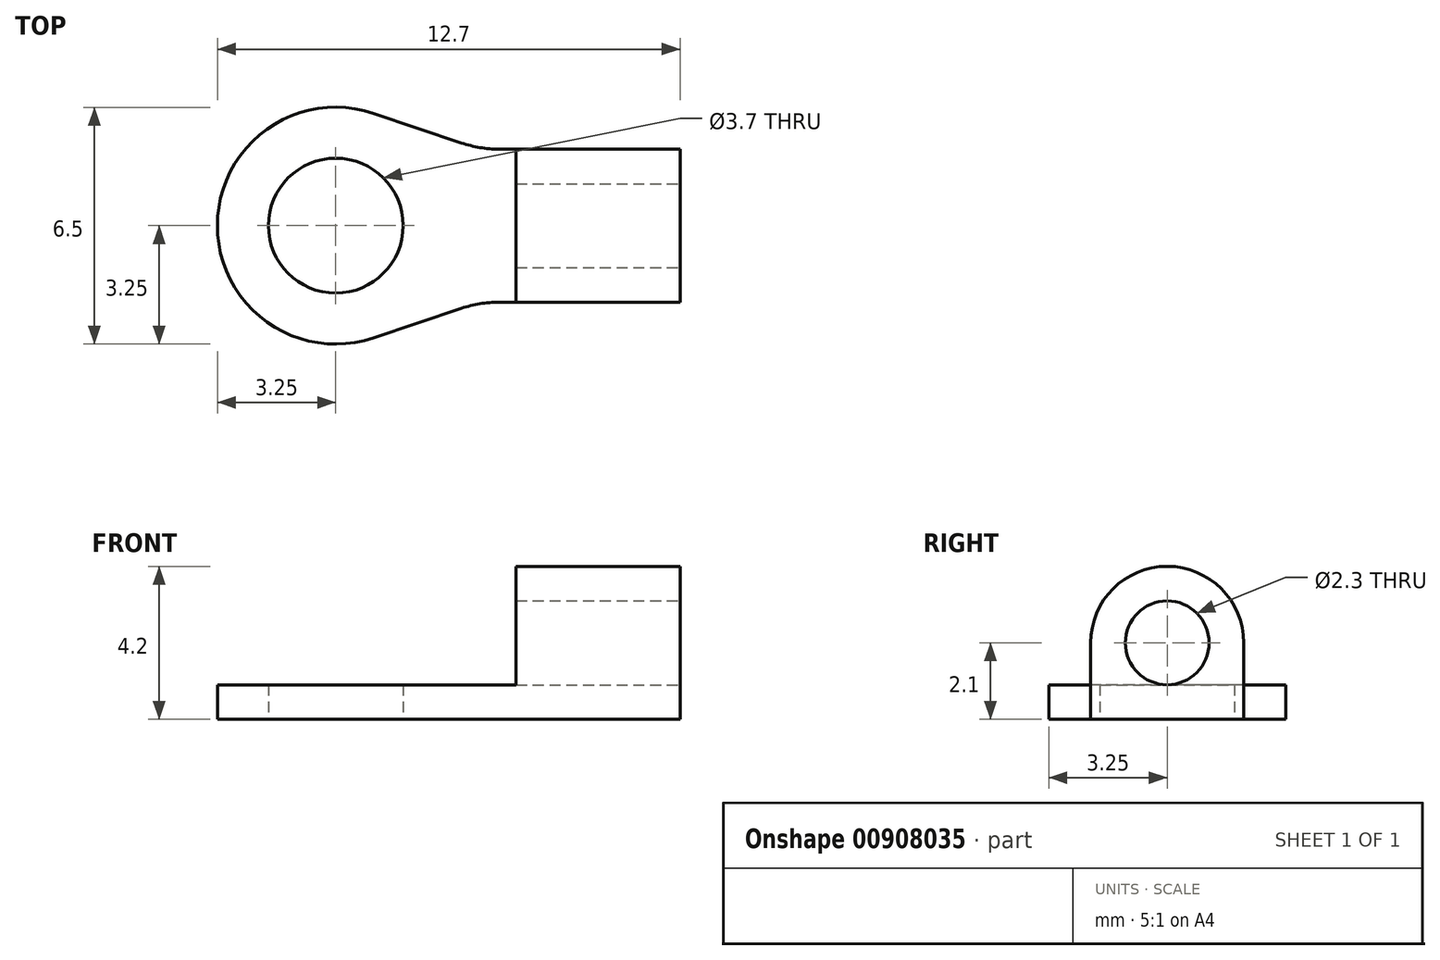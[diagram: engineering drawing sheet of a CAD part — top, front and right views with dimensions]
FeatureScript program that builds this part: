
annotation { "Feature Type Name" : "Feature", "Feature Type Description" : "" }
export const myFeature = defineFeature(function(context is Context, id is Id, definition is map)
    precondition{}
    {
        {
            var Q0;
            Q0=qCreatedBy(makeId("Top.planeOp"),FACE);
            var sketch = newSketch(context, id + "F0", { "sketchPlane" : qUnion([Q0])});
            skLineSegment(sketch, "E0.left", {"start": v(0, 3.25) * mm, "end": v(0, 3.25) * mm});
            skLineSegment(sketch, "E0.right", {"start": v(12.7, 1.15) * mm, "end": v(12.7, 5.35) * mm});
            skPoint(sketch, "E1.visualSharp", {"position": v(0, 6.5) * mm});
            skArc(sketch, "E1.filletArc", {"start": v(3.25, 6.5) * mm, "mid": v(0.95, 5.55) * mm, "end": v(0, 3.25) * mm});
            skPoint(sketch, "E2.visualSharp", {"position": v(0, 0) * mm});
            skArc(sketch, "E2.filletArc", {"start": v(0, 3.25) * mm, "mid": v(0.95, 0.95) * mm, "end": v(3.25, 0) * mm});
            skLineSegment(sketch, "E3.bottom", {"start": v(12.7, 1.15) * mm, "end": v(8.2, 1.15) * mm});
            skLineSegment(sketch, "E3.top", {"start": v(12.7, 5.35) * mm, "end": v(8.2, 5.35) * mm});
            skPoint(sketch, "E3.middle", {"position": v(12.7, 3.25) * mm});
            skArc(sketch, "E4", {"start": v(4.29, 6.33) * mm, "mid": v(0, 3.25) * mm, "end": v(4.29, 0.17) * mm});
            skCircle(sketch, "E5", {"center": v(3.25, 3.25) * mm, "radius": 1.85 * mm});
            skLineSegment(sketch, "E6", {"start": v(8.2, 5.35) * mm, "end": v(7.73, 5.35) * mm});
            skLineSegment(sketch, "E7", {"start": v(7.73, 1.15) * mm, "end": v(8.2, 1.15) * mm});
            skLineSegment(sketch, "E8", {"start": v(6.7, 5.52) * mm, "end": v(4.29, 6.33) * mm});
            skLineSegment(sketch, "E9", {"start": v(6.7, 0.98) * mm, "end": v(4.29, 0.17) * mm});
            skPoint(sketch, "E10.orphan", {"position": v(17.2, 5.35) * mm});
            skPoint(sketch, "E11.orphan", {"position": v(17.2, 1.15) * mm});
            skPoint(sketch, "E0.top.end.orphan", {"position": v(12.7, 6.5) * mm});
            skPoint(sketch, "E0.bottom.end.orphan", {"position": v(12.7, 0) * mm});
            skPoint(sketch, "E12.visualSharp", {"position": v(7.2, 5.35) * mm});
            skArc(sketch, "E12.filletArc", {"start": v(6.7, 5.52) * mm, "mid": v(7.2, 5.4) * mm, "end": v(7.73, 5.35) * mm});
            skPoint(sketch, "E13.visualSharp", {"position": v(7.2, 1.15) * mm});
            skArc(sketch, "E13.filletArc", {"start": v(7.73, 1.15) * mm, "mid": v(7.2, 1.1) * mm, "end": v(6.7, 0.98) * mm});
            skSolve(sketch);
        }
        {
            var Q0;
            Q0=makeQuery(id+"F0.imprint","IMPRINT",FACE,{"disambiguationData":[TD([[makeQuery(id+"F0.imprint","IMPRINT",EDGE,{"derivedFrom":sQuery(id+"F0.wireOp",EDGE,"E0.right")}),1.0]])]});
            extrude(context, id + "F1", {"entities" : qUnion([Q0]), "depth" : 0.95 * mm, "offsetDistance" : 25 * mm});
        }
        {
            var Q0;
            Q0=makeQuery(id+"F1.opExtrude","CAP_FACE",FACE,{"disambiguationData":[OSD([sQuery(id+"F0.wireOp",EDGE,"E0.right"),sQuery(id+"F0.wireOp",EDGE,"E3.bottom"),sQuery(id+"F0.wireOp",EDGE,"E3.top"),sQuery(id+"F0.wireOp",EDGE,"E4"),sQuery(id+"F0.wireOp",EDGE,"E5"),sQuery(id+"F0.wireOp",EDGE,"E6"),sQuery(id+"F0.wireOp",EDGE,"E7"),sQuery(id+"F0.wireOp",EDGE,"E8"),sQuery(id+"F0.wireOp",EDGE,"E9"),sQuery(id+"F0.wireOp",EDGE,"E12.filletArc"),sQuery(id+"F0.wireOp",EDGE,"E13.filletArc")])],"isStart":false});
            var sketch = newSketch(context, id + "F2", { "sketchPlane" : qUnion([Q0])});
            skLineSegment(sketch, "E14.bottom", {"start": v(12.7, 5.35) * mm, "end": v(8.2, 5.35) * mm});
            skLineSegment(sketch, "E14.top", {"start": v(12.7, 1.15) * mm, "end": v(8.2, 1.15) * mm});
            skLineSegment(sketch, "E14.left", {"start": v(12.7, 5.35) * mm, "end": v(12.7, 1.15) * mm});
            skLineSegment(sketch, "E14.right", {"start": v(8.2, 5.35) * mm, "end": v(8.2, 1.15) * mm});
            skSolve(sketch);
        }
        {
            var Q0;
            Q0=makeQuery(id+"F2.imprint","IMPRINT",FACE,{"disambiguationData":[TD([[makeQuery(id+"F2.imprint","IMPRINT",EDGE,{"derivedFrom":sQuery(id+"F2.wireOp",EDGE,"E14.bottom")}),1.0]])]});
            extrude(context, id + "F3", {"entities" : qUnion([Q0]), "operationType" : NewBodyOperationType.ADD, "depth" : 3.25 * mm, "offsetDistance" : 25 * mm});
        }
        {
            var Q0;
            Q0=makeQuery(id+"F3.opExtrude","CAP_EDGE",EDGE,{"disambiguationData":[OSD([sQuery(id+"F2.wireOp",EDGE,"E14.bottom")])],"isStart":false});
            var Q1;
            Q1=makeQuery(id+"F3.opExtrude","CAP_EDGE",EDGE,{"disambiguationData":[OSD([sQuery(id+"F2.wireOp",EDGE,"E14.top")])],"isStart":false});
            fillet(context, id + "F4", {"entities" : qUnion([Q0, Q1]), "radius" : 2.1 * mm, "tangentPropagation" : true, "allowEdgeOverflow" : false});
        }
        {
            var Q0;
            Q0=makeQuery(id+"F3.boolean.opBoolean","MERGE",FACE,{"derivedFrom":[makeQuery(id+"F1.opExtrude","SWEPT_FACE",FACE,{"disambiguationData":[OSD([sQuery(id+"F0.wireOp",EDGE,"E0.right")])]}),makeQuery(id+"F3.opExtrude","SWEPT_FACE",FACE,{"disambiguationData":[OSD([sQuery(id+"F2.wireOp",EDGE,"E14.left")])]})]});
            var sketch = newSketch(context, id + "F5", { "sketchPlane" : qUnion([Q0])});
            skCircle(sketch, "E15", {"center": v(3.25, 2.1) * mm, "radius": 1.15 * mm});
            skSolve(sketch);
        }
        {
            var Q0;
            Q0=makeQuery(id+"F5.imprint","IMPRINT",FACE,{"disambiguationData":[TD([[makeQuery(id+"F5.imprint","IMPRINT",EDGE,{"derivedFrom":sQuery(id+"F5.wireOp",EDGE,"E15")}),1.0]])]});
            extrude(context, id + "F6", {"entities" : qUnion([Q0]), "operationType" : NewBodyOperationType.REMOVE, "oppositeDirection" : true, "depth" : 25 * mm, "offsetDistance" : 25 * mm});
        }
    });
